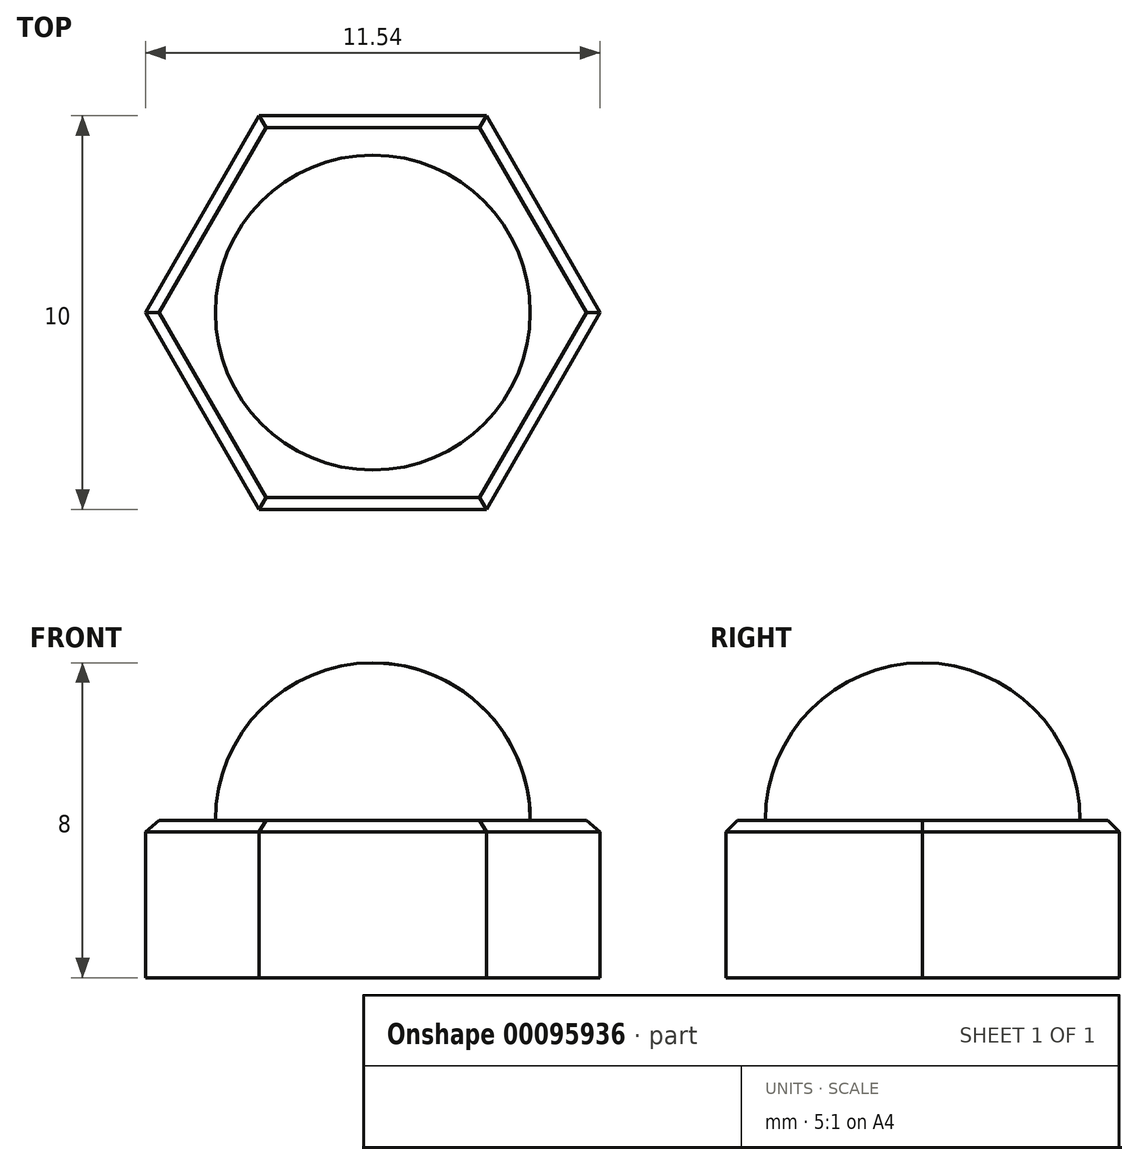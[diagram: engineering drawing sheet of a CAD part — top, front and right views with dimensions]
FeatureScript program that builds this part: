
annotation { "Feature Type Name" : "Feature", "Feature Type Description" : "" }
export const myFeature = defineFeature(function(context is Context, id is Id, definition is map)
    precondition{}
    {
        {
            var Q0;
            Q0=qCreatedBy(makeId("Top.planeOp"),FACE);
            var sketch = newSketch(context, id + "F0", { "sketchPlane" : qUnion([Q0])});
            skCircle(sketch, "E0.cCircle", {"center": v(0, 0) * mm, "radius": 5 * mm, "construction": true});
            skLineSegment(sketch, "E0.0", {"start": v(-2.89, 5) * mm, "end": v(2.89, 5) * mm});
            skLineSegment(sketch, "E0.1", {"start": v(2.89, 5) * mm, "end": v(5.77, 0) * mm});
            skLineSegment(sketch, "E0.2", {"start": v(5.77, 0) * mm, "end": v(2.89, -5) * mm});
            skLineSegment(sketch, "E0.3", {"start": v(2.89, -5) * mm, "end": v(-2.89, -5) * mm});
            skLineSegment(sketch, "E0.4", {"start": v(-2.89, -5) * mm, "end": v(-5.77, 0) * mm});
            skLineSegment(sketch, "E0.5", {"start": v(-5.77, 0) * mm, "end": v(-2.89, 5) * mm});
            skPoint(sketch, "E0.0.midPoint", {"position": v(0, 5) * mm});
            skSolve(sketch);
        }
        {
            var Q0;
            Q0 = qSketchRegion(id + "F0", true);
            extrude(context, id + "F1", {"entities" : qUnion([Q0]), "depth" : 4 * mm});
        }
        {
            var Q0;
            Q0=makeQuery(id+"F1.opExtrude","CAP_EDGE",EDGE,{"disambiguationData":[OSD([sQuery(id+"F0.wireOp",EDGE,"E0.2")])],"isStart":false});
            var Q1;
            Q1=makeQuery(id+"F1.opExtrude","CAP_EDGE",EDGE,{"disambiguationData":[OSD([sQuery(id+"F0.wireOp",EDGE,"E0.3")])],"isStart":false});
            var Q2;
            Q2=makeQuery(id+"F1.opExtrude","CAP_EDGE",EDGE,{"disambiguationData":[OSD([sQuery(id+"F0.wireOp",EDGE,"E0.1")])],"isStart":false});
            var Q3;
            Q3=makeQuery(id+"F1.opExtrude","CAP_EDGE",EDGE,{"disambiguationData":[OSD([sQuery(id+"F0.wireOp",EDGE,"E0.4")])],"isStart":false});
            var Q4;
            Q4=makeQuery(id+"F1.opExtrude","CAP_EDGE",EDGE,{"disambiguationData":[OSD([sQuery(id+"F0.wireOp",EDGE,"E0.5")])],"isStart":false});
            var Q5;
            Q5=makeQuery(id+"F1.opExtrude","CAP_EDGE",EDGE,{"disambiguationData":[OSD([sQuery(id+"F0.wireOp",EDGE,"E0.0")])],"isStart":false});
            chamfer(context, id + "F2", {"entities" : qUnion([Q0, Q1, Q2, Q3, Q4, Q5]), "width" : 0.3 * mm, "tangentPropagation" : true});
        }
        {
            var Q0;
            Q0=makeQuery(id+"F1.opExtrude","CAP_FACE",FACE,{"disambiguationData":[OSD([sQuery(id+"F0.wireOp",EDGE,"E0.0"),sQuery(id+"F0.wireOp",EDGE,"E0.1"),sQuery(id+"F0.wireOp",EDGE,"E0.2"),sQuery(id+"F0.wireOp",EDGE,"E0.3"),sQuery(id+"F0.wireOp",EDGE,"E0.4"),sQuery(id+"F0.wireOp",EDGE,"E0.5")])],"isStart":false});
            var sketch = newSketch(context, id + "F3", { "sketchPlane" : qUnion([Q0])});
            skCircle(sketch, "E1", {"center": v(0, 0) * mm, "radius": 4 * mm});
            skSolve(sketch);
        }
        {
            var Q0;
            Q0=makeQuery(id+"F3.imprint","IMPRINT",FACE,{"disambiguationData":[TD([[makeQuery(id+"F3.imprint","IMPRINT",EDGE,{"derivedFrom":sQuery(id+"F3.wireOp",EDGE,"E1")}),1.0]])]});
            extrude(context, id + "F4", {"entities" : qUnion([Q0]), "operationType" : NewBodyOperationType.ADD, "depth" : 4 * mm});
        }
        {
            var Q0;
            Q0=makeQuery(id+"F4.opExtrude","CAP_EDGE",EDGE,{"disambiguationData":[OSD([sQuery(id+"F3.wireOp",EDGE,"E1")])],"isStart":false});
            fillet(context, id + "F5", {"entities" : qUnion([Q0]), "radius" : 4 * mm, "tangentPropagation" : true, "allowEdgeOverflow" : false});
        }
    });
